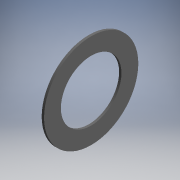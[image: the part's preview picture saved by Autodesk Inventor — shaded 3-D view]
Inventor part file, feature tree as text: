
AUTODESK INVENTOR PART (.ipt)
format: ipt  version: 2017.3 (Build 213256000, 256)  size: 95,744 bytes
history: native  units: mm (DEFAULTED — no unit token found)
features: other x7, revolve x1, sketch x1
ambient origin geometry x8: Origin, YZ Plane, XZ Plane, XY Plane, X Axis, Y Axis, Z Axis, Center Point
bodies: Solid1 (feature_tree)
feature tree (9):
  revolve  "Revolution1"  [1 undecoded]
  other  "ip_st_s2_XY"
  other  "ip_st_s2_YZ"
  other  "ip_st_s2_ZX"
  other  "ip_st_s2_X"
  other  "ip_st_s2_Y"
  other  "ip_st_s2_Z"
  other  "ip_st_s2_Center"
  sketch  "Sketch_1"  dims[d0=360.0deg d1=0.0mm]
note: 1 required parameter value undecoded (feature->parameter linkage not recoverable at this tier; creation-order binding heuristic only, values carry confidence <= 0.55)
